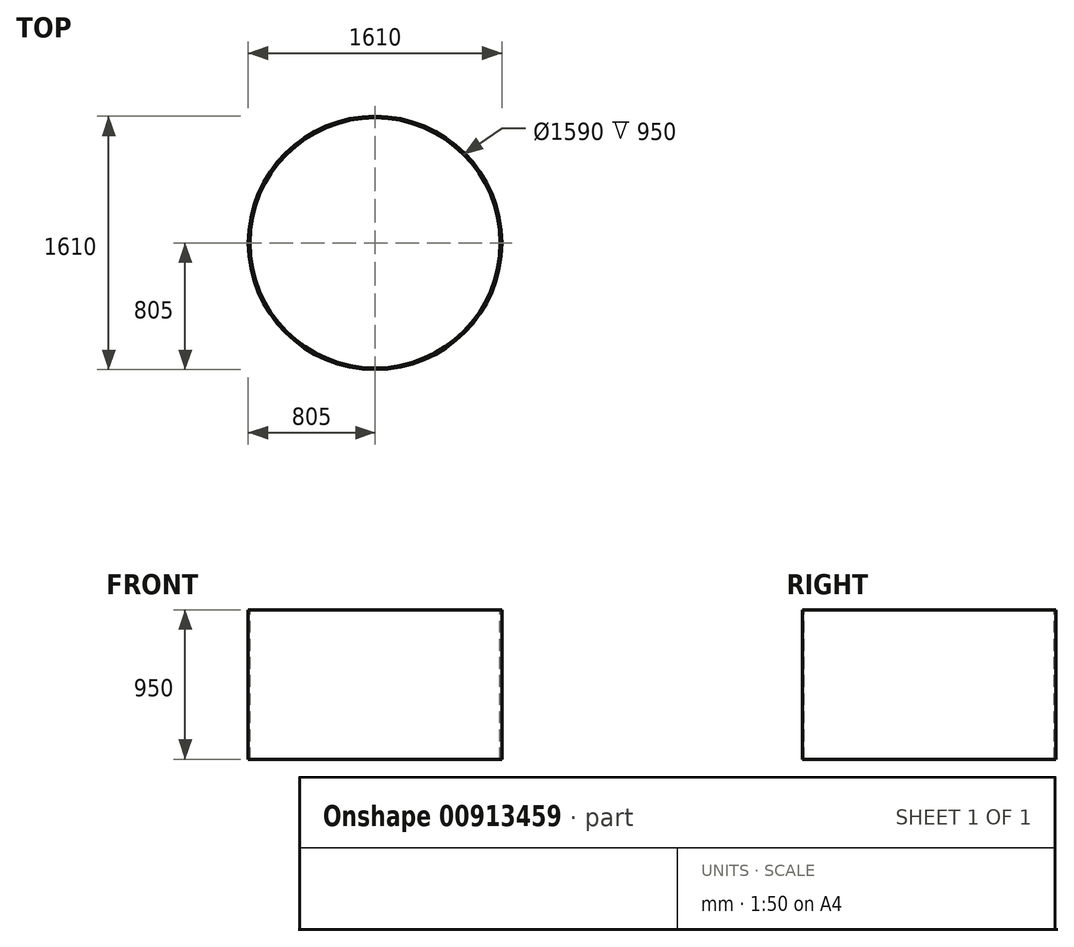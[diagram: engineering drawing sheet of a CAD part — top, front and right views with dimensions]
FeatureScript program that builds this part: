
annotation { "Feature Type Name" : "Feature", "Feature Type Description" : "" }
export const myFeature = defineFeature(function(context is Context, id is Id, definition is map)
    precondition{}
    {
        {
            var Q0;
            Q0=qCreatedBy(makeId("Top.planeOp"),FACE);
            var sketch = newSketch(context, id + "F0", { "sketchPlane" : qUnion([Q0])});
            skCircle(sketch, "E0", {"center": v(0, 0) * mm, "radius": 795 * mm});
            skCircle(sketch, "E1", {"center": v(0, 0) * mm, "radius": 805 * mm});
            skSolve(sketch);
        }
        {
            var Q0;
            Q0=makeQuery(id+"F0.imprint","IMPRINT",FACE,{"disambiguationData":[TD([[makeQuery(id+"F0.imprint","IMPRINT",EDGE,{"derivedFrom":sQuery(id+"F0.wireOp",EDGE,"E0")}),-1.0]])]});
            var Q1;
            Q1=makeQuery(id+"F0.imprint","IMPRINT",FACE,{"disambiguationData":[TD([[makeQuery(id+"F0.imprint","IMPRINT",EDGE,{"derivedFrom":sQuery(id+"F0.wireOp",EDGE,"E0")}),1.0]])]});
            extrude(context, id + "F1", {"entities" : qUnion([Q0, Q1]), "depth" : 950 * mm, "offsetDistance" : 25 * mm});
        }
        {
            var Q0;
            Q0=makeQuery(id+"F1.opExtrude","CAP_FACE",FACE,{"disambiguationData":[OSD([sQuery(id+"F0.wireOp",EDGE,"E1")])],"isStart":false});
            var sketch = newSketch(context, id + "F2", { "sketchPlane" : qUnion([Q0])});
            skCircle(sketch, "E2", {"center": v(0, 0) * mm, "radius": 795 * mm});
            skSolve(sketch);
        }
        {
            var Q0;
            Q0=makeQuery(id+"F2.imprint","IMPRINT",FACE,{"disambiguationData":[TD([[makeQuery(id+"F2.imprint","IMPRINT",EDGE,{"derivedFrom":sQuery(id+"F2.wireOp",EDGE,"E2")}),1.0]])]});
            extrude(context, id + "F3", {"entities" : qUnion([Q0]), "operationType" : NewBodyOperationType.REMOVE, "oppositeDirection" : true, "depth" : 2000 * mm, "offsetDistance" : 25 * mm});
        }
    });
